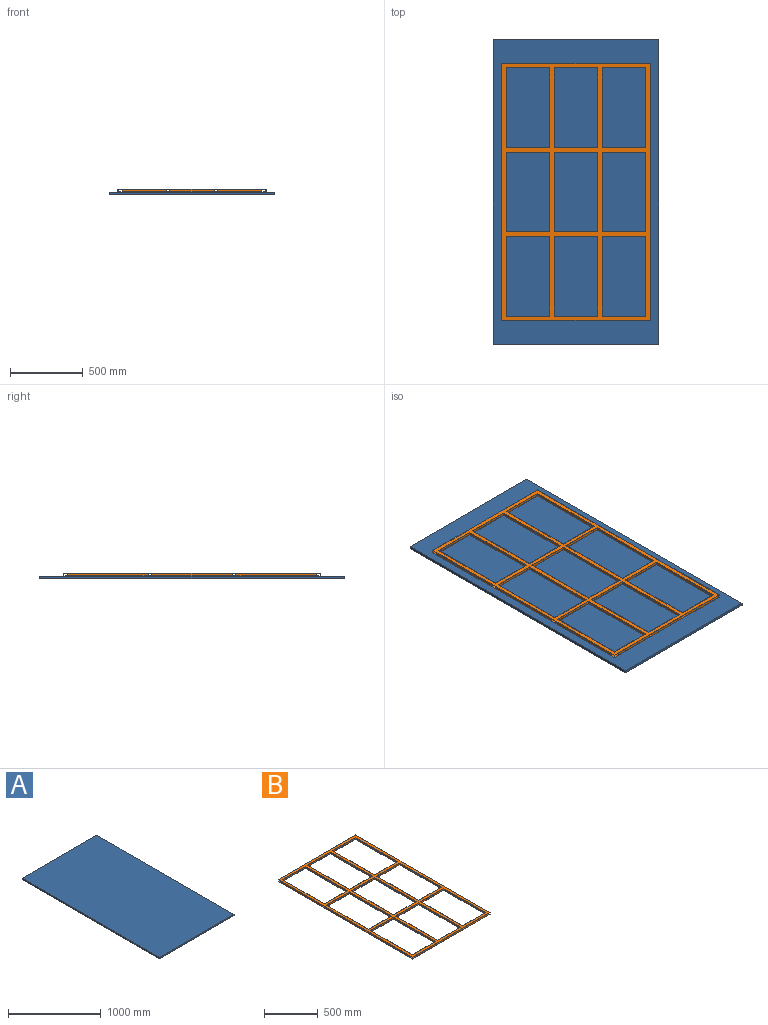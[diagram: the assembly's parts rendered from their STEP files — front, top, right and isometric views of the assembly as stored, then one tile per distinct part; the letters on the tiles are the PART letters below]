
ASSEMBLY  parts=2 mates=1
PART A: 6 faces, bbox 1140x2095x18 mm
  f0: plane 2095x18mm, normal (-1,0,0), area 37710mm2, adj f1,f3,f4,f5
  f1: plane 1140x18mm, normal (0,-1,0), area 20520mm2, adj f0,f2,f4,f5
  f2: plane 2095x18mm, normal (1,0,0), area 37710mm2, adj f1,f3,f4,f5
  f3: plane 1140x18mm, normal (0,1,0), area 20520mm2, adj f0,f2,f4,f5
  f4: plane 2095x1140mm, normal (0,0,-1), area 2388300mm2, adj f0,f1,f2,f3
  f5: plane 2095x1140mm, normal (0,0,1), area 2388300mm2, adj f0,f1,f2,f3
PART B: 124 faces, bbox 1020x1770x20 mm
  f0: plane 1770x20mm, normal (-1,0,0), area 33736mm2, adj f34,f35,f72,f73,f80,f82,f116,f117
  f1: plane 1770x20mm, normal (1,0,0), area 33736mm2, adj f34,f35,f72,f73,f80,f82,f92,f93
  f2: plane 554x16mm, normal (-1,0,0), area 8864mm2, adj f80,f82,f103,f106
  f3: plane 554x16mm, normal (-1,0,0), area 8864mm2, adj f80,f82,f101,f104
  f4: plane 554x16mm, normal (-1,0,0), area 8864mm2, adj f80,f82,f102,f105
  f5: plane 16x2mm, normal (-1,0,0), area 32mm2, adj f34,f80,f82,f100
  f6: plane 554x16mm, normal (1,0,0), area 8864mm2, adj f80,f82,f118,f123
  f7: plane 554x16mm, normal (1,0,0), area 8864mm2, adj f80,f82,f116,f121
  f8: plane 554x16mm, normal (1,0,0), area 8864mm2, adj f80,f82,f119,f120
  f9: plane 16x2mm, normal (1,0,0), area 32mm2, adj f34,f80,f82,f117
  f10: plane 554x16mm, normal (-1,0,0), area 8864mm2, adj f80,f82,f87,f90
  f11: plane 554x16mm, normal (-1,0,0), area 8864mm2, adj f80,f82,f85,f88
  f12: plane 554x16mm, normal (-1,0,0), area 8864mm2, adj f80,f82,f86,f89
  f13: plane 16x2mm, normal (-1,0,0), area 32mm2, adj f34,f80,f82,f84
  f14: plane 554x16mm, normal (1,0,0), area 8864mm2, adj f80,f82,f111,f114
  f15: plane 554x16mm, normal (1,0,0), area 8864mm2, adj f80,f82,f109,f112
  f16: plane 554x16mm, normal (1,0,0), area 8864mm2, adj f80,f82,f110,f113
  f17: plane 16x2mm, normal (1,0,0), area 32mm2, adj f34,f80,f82,f108
  f18: plane 554x16mm, normal (-1,0,0), area 8864mm2, adj f80,f82,f111,f114
  f19: plane 554x16mm, normal (-1,0,0), area 8864mm2, adj f80,f82,f109,f112
  f20: plane 554x16mm, normal (-1,0,0), area 8864mm2, adj f80,f82,f110,f113
  f21: plane 16x2mm, normal (-1,0,0), area 32mm2, adj f34,f80,f82,f108
  f22: plane 554x16mm, normal (1,0,0), area 8864mm2, adj f80,f82,f103,f106
  f23: plane 554x16mm, normal (1,0,0), area 8864mm2, adj f80,f82,f101,f104
  f24: plane 554x16mm, normal (1,0,0), area 8864mm2, adj f80,f82,f102,f105
  f25: plane 16x2mm, normal (1,0,0), area 32mm2, adj f34,f80,f82,f100
  f26: plane 554x16mm, normal (-1,0,0), area 8864mm2, adj f80,f82,f95,f98
  f27: plane 554x16mm, normal (-1,0,0), area 8864mm2, adj f80,f82,f93,f96
  f28: plane 554x16mm, normal (-1,0,0), area 8864mm2, adj f80,f82,f94,f97
  f29: plane 16x2mm, normal (-1,0,0), area 32mm2, adj f34,f80,f82,f92
  f30: plane 554x16mm, normal (1,0,0), area 8864mm2, adj f80,f82,f87,f90
  f31: plane 554x16mm, normal (1,0,0), area 8864mm2, adj f80,f82,f85,f88
  f32: plane 554x16mm, normal (1,0,0), area 8864mm2, adj f80,f82,f86,f89
  f33: plane 16x2mm, normal (1,0,0), area 32mm2, adj f34,f80,f82,f84
  f34: plane 1020x20mm, normal (0,1,0), area 18736mm2, adj f0,f1,f5,f9,f13,f17,f21,f25
  f35: plane 1020x20mm, normal (0,-1,0), area 18736mm2, adj f0,f1,f72,f73,f74,f75,f76,f77
  f36: plane 550x20mm, normal (1,0,0), area 11000mm2, adj f37,f63,f72,f73
  f37: plane 300x20mm, normal (0,-1,0), area 6000mm2, adj f36,f38,f72,f73
  f38: plane 550x20mm, normal (-1,0,0), area 11000mm2, adj f37,f63,f72,f73
  f39: plane 550x20mm, normal (1,0,0), area 11000mm2, adj f40,f64,f72,f73
  f40: plane 300x20mm, normal (0,-1,0), area 6000mm2, adj f39,f41,f72,f73
  f41: plane 550x20mm, normal (-1,0,0), area 11000mm2, adj f40,f64,f72,f73
  f42: plane 300x20mm, normal (0,1,0), area 6000mm2, adj f43,f65,f72,f73
  f43: plane 550x20mm, normal (1,0,0), area 11000mm2, adj f42,f44,f72,f73
  f44: plane 300x20mm, normal (0,-1,0), area 6000mm2, adj f43,f65,f72,f73
  f45: plane 550x20mm, normal (1,0,0), area 11000mm2, adj f46,f66,f72,f73
  f46: plane 300x20mm, normal (0,-1,0), area 6000mm2, adj f45,f47,f72,f73
  f47: plane 550x20mm, normal (-1,0,0), area 11000mm2, adj f46,f66,f72,f73
  f48: plane 300x20mm, normal (0,-1,0), area 6000mm2, adj f49,f67,f72,f73
  f49: plane 550x20mm, normal (-1,0,0), area 11000mm2, adj f48,f50,f72,f73
  f50: plane 300x20mm, normal (0,1,0), area 6000mm2, adj f49,f67,f72,f73
  f51: plane 300x20mm, normal (0,-1,0), area 6000mm2, adj f52,f68,f72,f73
  f52: plane 550x20mm, normal (-1,0,0), area 11000mm2, adj f51,f53,f72,f73
  f53: plane 300x20mm, normal (0,1,0), area 6000mm2, adj f52,f68,f72,f73
  f54: plane 550x20mm, normal (1,0,0), area 11000mm2, adj f55,f69,f72,f73
  f55: plane 300x20mm, normal (0,-1,0), area 6000mm2, adj f54,f56,f72,f73
  f56: plane 550x20mm, normal (-1,0,0), area 11000mm2, adj f55,f69,f72,f73
  f57: plane 550x20mm, normal (1,0,0), area 11000mm2, adj f58,f70,f72,f73
  f58: plane 300x20mm, normal (0,-1,0), area 6000mm2, adj f57,f59,f72,f73
  f59: plane 550x20mm, normal (-1,0,0), area 11000mm2, adj f58,f70,f72,f73
  f60: plane 550x20mm, normal (1,0,0), area 11000mm2, adj f61,f71,f72,f73
  f61: plane 300x20mm, normal (0,-1,0), area 6000mm2, adj f60,f62,f72,f73
  f62: plane 550x20mm, normal (-1,0,0), area 11000mm2, adj f61,f71,f72,f73
  f63: plane 300x20mm, normal (0,1,0), area 6000mm2, adj f36,f38,f72,f73
  f64: plane 300x20mm, normal (0,1,0), area 6000mm2, adj f39,f41,f72,f73
  f65: plane 550x20mm, normal (-1,0,0), area 11000mm2, adj f42,f44,f72,f73
  f66: plane 300x20mm, normal (0,1,0), area 6000mm2, adj f45,f47,f72,f73
  f67: plane 550x20mm, normal (1,0,0), area 11000mm2, adj f48,f50,f72,f73
  f68: plane 550x20mm, normal (1,0,0), area 11000mm2, adj f51,f53,f72,f73
  f69: plane 300x20mm, normal (0,1,0), area 6000mm2, adj f54,f56,f72,f73
  f70: plane 300x20mm, normal (0,1,0), area 6000mm2, adj f57,f59,f72,f73
  f71: plane 300x20mm, normal (0,1,0), area 6000mm2, adj f60,f62,f72,f73
  f72: plane 1770x1020mm, normal (0,0,1), area 320400mm2, adj f0,f1,f34,f35,f36,f37,f38,f39
  f73: plane 1770x1020mm, normal (0,0,-1), area 320400mm2, adj f0,f1,f34,f35,f36,f37,f38,f39
  f74: plane 16x2mm, normal (-1,0,0), area 32mm2, adj f35,f80,f82,f107
  f75: plane 16x2mm, normal (1,0,0), area 32mm2, adj f35,f80,f82,f122
  f76: plane 16x2mm, normal (-1,0,0), area 32mm2, adj f35,f80,f82,f91
  f77: plane 16x2mm, normal (1,0,0), area 32mm2, adj f35,f80,f82,f115
  f78: plane 16x2mm, normal (-1,0,0), area 32mm2, adj f35,f80,f82,f115
  f79: plane 16x2mm, normal (1,0,0), area 32mm2, adj f35,f80,f82,f107
  f80: plane 1770x1020mm, normal (0,0,-1), area 279344mm2, adj f0,f1,f2,f3,f4,f5,f6,f7
  f81: plane 16x2mm, normal (-1,0,0), area 32mm2, adj f35,f80,f82,f99
  f82: plane 1770x1020mm, normal (0,0,1), area 279344mm2, adj f0,f1,f2,f3,f4,f5,f6,f7
  f83: plane 16x2mm, normal (1,0,0), area 32mm2, adj f35,f80,f82,f91
  f84: plane 304x16mm, normal (0,-1,0), area 4864mm2, adj f13,f33,f80,f82
  f85: plane 304x16mm, normal (0,1,0), area 4864mm2, adj f11,f31,f80,f82
  f86: plane 304x16mm, normal (0,-1,0), area 4864mm2, adj f12,f32,f80,f82
  f87: plane 304x16mm, normal (0,1,0), area 4864mm2, adj f10,f30,f80,f82
  f88: plane 304x16mm, normal (0,-1,0), area 4864mm2, adj f11,f31,f80,f82
  f89: plane 304x16mm, normal (0,1,0), area 4864mm2, adj f12,f32,f80,f82
  f90: plane 304x16mm, normal (0,-1,0), area 4864mm2, adj f10,f30,f80,f82
  f91: plane 304x16mm, normal (0,1,0), area 4864mm2, adj f76,f80,f82,f83
  f92: plane 16x2mm, normal (0,-1,0), area 32mm2, adj f1,f29,f80,f82
  f93: plane 16x2mm, normal (0,1,0), area 32mm2, adj f1,f27,f80,f82
  f94: plane 16x2mm, normal (0,-1,0), area 32mm2, adj f1,f28,f80,f82
  f95: plane 16x2mm, normal (0,1,0), area 32mm2, adj f1,f26,f80,f82
  f96: plane 16x2mm, normal (0,-1,0), area 32mm2, adj f1,f27,f80,f82
  f97: plane 16x2mm, normal (0,1,0), area 32mm2, adj f1,f28,f80,f82
  f98: plane 16x2mm, normal (0,-1,0), area 32mm2, adj f1,f26,f80,f82
  f99: plane 16x2mm, normal (0,1,0), area 32mm2, adj f1,f80,f81,f82
  f100: plane 304x16mm, normal (0,-1,0), area 4864mm2, adj f5,f25,f80,f82
  f101: plane 304x16mm, normal (0,1,0), area 4864mm2, adj f3,f23,f80,f82
  f102: plane 304x16mm, normal (0,-1,0), area 4864mm2, adj f4,f24,f80,f82
  f103: plane 304x16mm, normal (0,1,0), area 4864mm2, adj f2,f22,f80,f82
  f104: plane 304x16mm, normal (0,-1,0), area 4864mm2, adj f3,f23,f80,f82
  f105: plane 304x16mm, normal (0,1,0), area 4864mm2, adj f4,f24,f80,f82
  f106: plane 304x16mm, normal (0,-1,0), area 4864mm2, adj f2,f22,f80,f82
  f107: plane 304x16mm, normal (0,1,0), area 4864mm2, adj f74,f79,f80,f82
  f108: plane 304x16mm, normal (0,-1,0), area 4864mm2, adj f17,f21,f80,f82
  f109: plane 304x16mm, normal (0,1,0), area 4864mm2, adj f15,f19,f80,f82
  f110: plane 304x16mm, normal (0,-1,0), area 4864mm2, adj f16,f20,f80,f82
  f111: plane 304x16mm, normal (0,1,0), area 4864mm2, adj f14,f18,f80,f82
  f112: plane 304x16mm, normal (0,-1,0), area 4864mm2, adj f15,f19,f80,f82
  f113: plane 304x16mm, normal (0,1,0), area 4864mm2, adj f16,f20,f80,f82
  f114: plane 304x16mm, normal (0,-1,0), area 4864mm2, adj f14,f18,f80,f82
  f115: plane 304x16mm, normal (0,1,0), area 4864mm2, adj f77,f78,f80,f82
  f116: plane 16x2mm, normal (0,1,0), area 32mm2, adj f0,f7,f80,f82
  f117: plane 16x2mm, normal (0,-1,0), area 32mm2, adj f0,f9,f80,f82
  f118: plane 16x2mm, normal (0,1,0), area 32mm2, adj f0,f6,f80,f82
  f119: plane 16x2mm, normal (0,-1,0), area 32mm2, adj f0,f8,f80,f82
  f120: plane 16x2mm, normal (0,1,0), area 32mm2, adj f0,f8,f80,f82
  f121: plane 16x2mm, normal (0,-1,0), area 32mm2, adj f0,f7,f80,f82
  f122: plane 16x2mm, normal (0,1,0), area 32mm2, adj f0,f75,f80,f82
  f123: plane 16x2mm, normal (0,-1,0), area 32mm2, adj f0,f6,f80,f82
PLACE A t=(0,0,-10)mm
PLACE B t=(-480,90,-10)mm
MATE planar A.f5 <-> B.f73  axis (0,0,1) through (0,0,-10)mm
